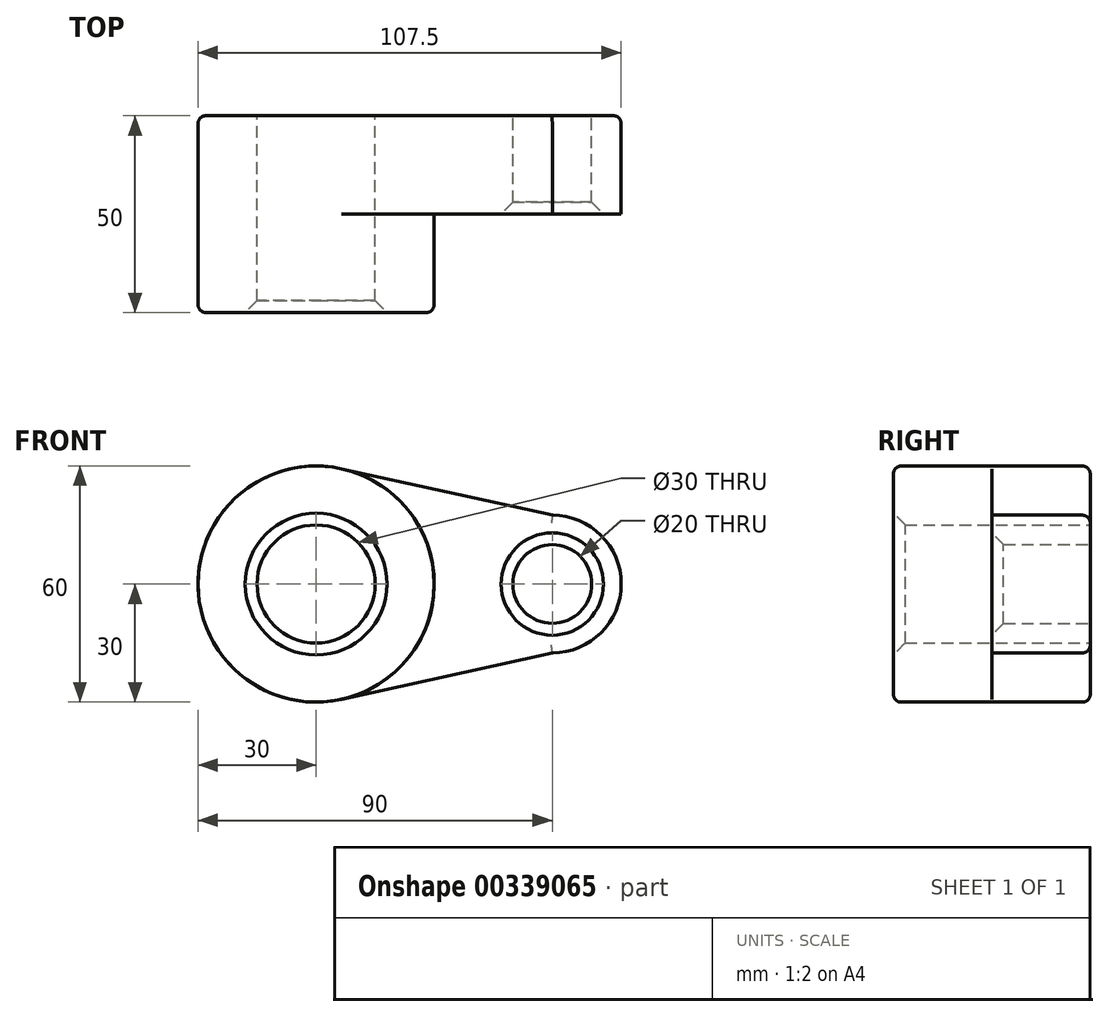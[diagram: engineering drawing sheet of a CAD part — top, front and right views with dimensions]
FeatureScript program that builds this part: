
annotation { "Feature Type Name" : "Feature", "Feature Type Description" : "" }
export const myFeature = defineFeature(function(context is Context, id is Id, definition is map)
    precondition{}
    {
        {
            var Q0;
            Q0=qCreatedBy(makeId("Front.planeOp"),FACE);
            var sketch = newSketch(context, id + "F0", { "sketchPlane" : qUnion([Q0])});
            skCircle(sketch, "E0", {"center": v(0, 0) * mm, "radius": 30 * mm});
            skCircle(sketch, "E1", {"center": v(60, 0) * mm, "radius": 17.5 * mm});
            skLineSegment(sketch, "E2", {"start": v(6.45, 29.3) * mm, "end": v(60, 17.5) * mm});
            skCircle(sketch, "E3", {"center": v(0, 0) * mm, "radius": 15 * mm});
            skCircle(sketch, "E4", {"center": v(60, 0) * mm, "radius": 10 * mm});
            skLineSegment(sketch, "E5", {"start": v(6.45, -29.3) * mm, "end": v(60, -17.5) * mm});
            skSolve(sketch);
        }
        {
            var Q0;
            Q0 = qSketchRegion(id + "F0", true);
            extrude(context, id + "F1", {"entities" : qUnion([Q0]), "depth" : 25 * mm});
        }
        {
            var Q0;
            Q0=makeQuery(id+"F0.imprint","IMPRINT",FACE,{"disambiguationData":[TD([[makeQuery(id+"F0.imprint","IMPRINT",EDGE,{"derivedFrom":sQuery(id+"F0.wireOp",EDGE,"E3")}),-1.0]])]});
            extrude(context, id + "F2", {"entities" : qUnion([Q0]), "operationType" : NewBodyOperationType.ADD, "depth" : 50 * mm});
        }
        {
            var Q0;
            Q0=makeQuery(id+"F1.opExtrude","CAP_EDGE",EDGE,{"disambiguationData":[OSD([sQuery(id+"F0.wireOp",EDGE,"E5")])],"isStart":true});
            var Q1;
            Q1=makeQuery(id+"F2.opExtrude","CAP_EDGE",EDGE,{"disambiguationData":[OSD([sQuery(id+"F0.wireOp",EDGE,"E0")])],"isStart":false});
            var Q2;
            Q2=makeQuery(id+"F1.opExtrude","CAP_EDGE",EDGE,{"disambiguationData":[OSD([sQuery(id+"F0.wireOp",EDGE,"E1")])],"isStart":true});
            var Q3;
            Q3=makeQuery(id+"F1.opExtrude","CAP_EDGE",EDGE,{"disambiguationData":[OSD([sQuery(id+"F0.wireOp",EDGE,"E0")])],"isStart":true});
            var Q4;
            Q4=makeQuery(id+"F1.opExtrude","CAP_EDGE",EDGE,{"disambiguationData":[OSD([sQuery(id+"F0.wireOp",EDGE,"E2")])],"isStart":true});
            fillet(context, id + "F3", {"entities" : qUnion([Q0, Q1, Q2, Q3, Q4]), "radius" : 2 * mm, "tangentPropagation" : true, "allowEdgeOverflow" : false});
        }
        {
            var Q0;
            Q0=makeQuery(id+"F2.opExtrude","CAP_EDGE",EDGE,{"disambiguationData":[OSD([sQuery(id+"F0.wireOp",EDGE,"E3")])],"isStart":false});
            var Q1;
            Q1=makeQuery(id+"F1.opExtrude","CAP_EDGE",EDGE,{"disambiguationData":[OSD([sQuery(id+"F0.wireOp",EDGE,"E4")])],"isStart":false});
            chamfer(context, id + "F4", {"entities" : qUnion([Q0, Q1]), "width" : 3 * mm, "tangentPropagation" : true});
        }
    });
